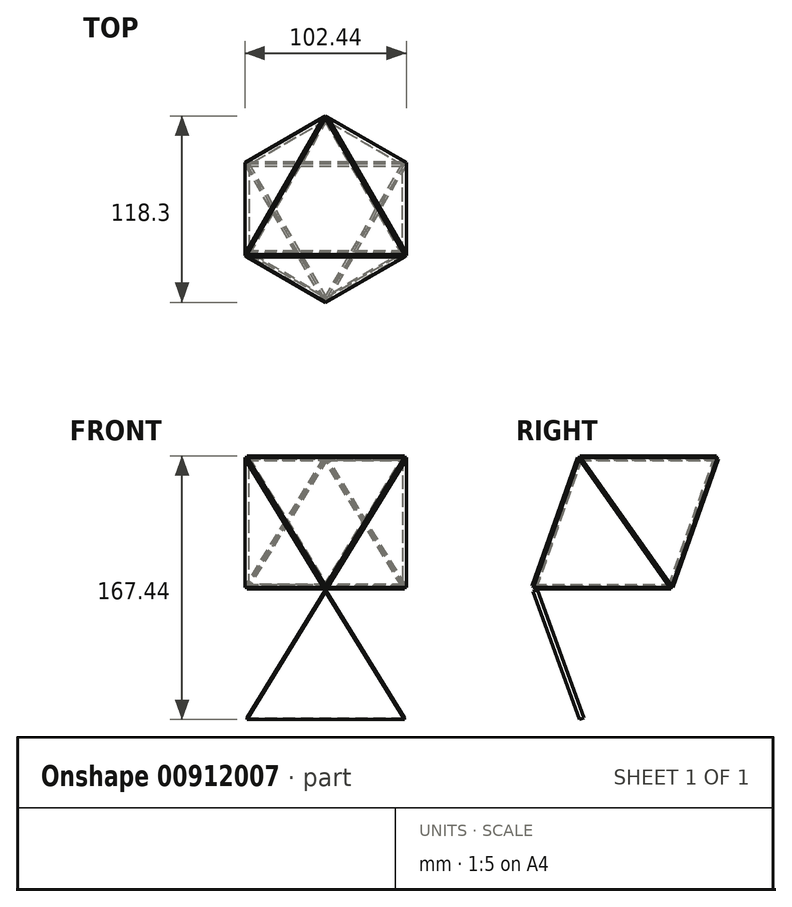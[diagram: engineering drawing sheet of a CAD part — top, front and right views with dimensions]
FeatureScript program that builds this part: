
annotation { "Feature Type Name" : "Feature", "Feature Type Description" : "" }
export const myFeature = defineFeature(function(context is Context, id is Id, definition is map)
    precondition{}
    {
        {
            var Q0;
            Q0=qCreatedBy(makeId("Top.planeOp"),FACE);
            var sketch = newSketch(context, id + "F0", { "sketchPlane" : qUnion([Q0])});
            skCircle(sketch, "E0.cCircle", {"center": v(0, 0) * mm, "radius": 28.87 * mm, "construction": true});
            skLineSegment(sketch, "E0.0", {"start": v(-50, 28.87) * mm, "end": v(50, 28.87) * mm});
            skLineSegment(sketch, "E0.1", {"start": v(50, 28.87) * mm, "end": v(0, -57.74) * mm});
            skLineSegment(sketch, "E0.2", {"start": v(0, -57.74) * mm, "end": v(-50, 28.87) * mm});
            skPoint(sketch, "E0.0.midPoint", {"position": v(0, 28.87) * mm});
            skSolve(sketch);
        }
        {
            var Q0;
            Q0=makeQuery(id+"F0.imprint","IMPRINT",FACE,{"disambiguationData":[TD([[makeQuery(id+"F0.imprint","IMPRINT",EDGE,{"derivedFrom":sQuery(id+"F0.wireOp",EDGE,"E0.0")}),-1.0]])]});
            extrude(context, id + "F1", {"entities" : qUnion([Q0]), "depth" : 3 * mm, "offsetDistance" : 25 * mm});
        }
        {
            var Q0;
            Q0=makeQuery(id+"F1.opExtrude","SWEPT_FACE",FACE,{"disambiguationData":[OSD([sQuery(id+"F0.wireOp",EDGE,"E0.2")])]});
            var sketch = newSketch(context, id + "F2", { "sketchPlane" : qUnion([Q0])});
            skLineSegment(sketch, "E1", {"start": v(-50, 1.5) * mm, "end": v(50, 1.5) * mm});
            skSolve(sketch);
        }
        {
            var Q0;
            Q0=makeQuery(id+"F1.opExtrude","SWEPT_BODY",BODY,{"disambiguationData":[OSD([sQuery(id+"F0.wireOp",EDGE,"E0.0"),sQuery(id+"F0.wireOp",EDGE,"E0.1"),sQuery(id+"F0.wireOp",EDGE,"E0.2")])]});
            transform(context, id + "F3", {"entities" : qUnion([Q0]), "transformType" : TransformType.TRANSLATION_3D, "dx" : 0 * mm, "dy" : 0 * mm, "dz" : 0 * mm, "makeCopy" : true});
        }
        {
            var Q0;
            Q0=makeQuery(id+"F3.opPattern","COPY",BODY,{"derivedFrom":makeQuery(id+"F1.opExtrude","SWEPT_BODY",BODY,{"disambiguationData":[OSD([sQuery(id+"F0.wireOp",EDGE,"E0.0"),sQuery(id+"F0.wireOp",EDGE,"E0.1"),sQuery(id+"F0.wireOp",EDGE,"E0.2")])]}),"instanceName":"1"});
            var Q1;
            Q1=sQuery(id+"F2.wireOp",EDGE,"E1");
            var Q2;
            Q2=sQuery(id+"F2.wireOp",EDGE,"E1");
            transform(context, id + "F4", {"entities" : qUnion([Q0]), "transformType" : TransformType.ROTATION, "transformAxis" : qUnion([Q2]), "angle" : 109.47 * degree, "makeCopy" : false});
        }
        {
            var Q0;
            Q0=makeQuery(id+"F1.opExtrude","SWEPT_BODY",BODY,{"disambiguationData":[OSD([sQuery(id+"F0.wireOp",EDGE,"E0.0"),sQuery(id+"F0.wireOp",EDGE,"E0.1"),sQuery(id+"F0.wireOp",EDGE,"E0.2")])]});
            transform(context, id + "F5", {"entities" : qUnion([Q0]), "transformType" : TransformType.TRANSLATION_3D, "dx" : 0 * mm, "dy" : 0 * mm, "dz" : 0 * mm, "makeCopy" : true});
        }
        {
            var Q0;
            Q0=makeQuery(id+"F1.opExtrude","SWEPT_FACE",FACE,{"disambiguationData":[OSD([sQuery(id+"F0.wireOp",EDGE,"E0.0")])]});
            var sketch = newSketch(context, id + "F6", { "sketchPlane" : qUnion([Q0])});
            skLineSegment(sketch, "E2", {"start": v(50, 1.5) * mm, "end": v(-50, 1.5) * mm});
            skSolve(sketch);
        }
        {
            var Q0;
            Q0=makeQuery(id+"F5.opPattern","COPY",BODY,{"derivedFrom":makeQuery(id+"F1.opExtrude","SWEPT_BODY",BODY,{"disambiguationData":[OSD([sQuery(id+"F0.wireOp",EDGE,"E0.0"),sQuery(id+"F0.wireOp",EDGE,"E0.1"),sQuery(id+"F0.wireOp",EDGE,"E0.2")])]}),"instanceName":"1"});
            var Q1;
            Q1=sQuery(id+"F6.wireOp",EDGE,"E2");
            var Q2;
            Q2=sQuery(id+"F6.wireOp",EDGE,"E2");
            transform(context, id + "F7", {"entities" : qUnion([Q0]), "transformType" : TransformType.ROTATION, "transformAxis" : qUnion([Q2]), "angle" : 109.47 * degree, "oppositeDirection" : true, "makeCopy" : false});
        }
        {
            var Q0;
            Q0=qCreatedBy(makeId("Front.planeOp"),FACE);
            var sketch = newSketch(context, id + "F8", { "sketchPlane" : qUnion([Q0])});
            skLineSegment(sketch, "E3", {"start": v(0, 0) * mm, "end": v(0, 75.98) * mm});
            skSolve(sketch);
        }
        {
            var Q0;
            Q0=makeQuery(id+"F3.opPattern","COPY",BODY,{"derivedFrom":makeQuery(id+"F1.opExtrude","SWEPT_BODY",BODY,{"disambiguationData":[OSD([sQuery(id+"F0.wireOp",EDGE,"E0.0"),sQuery(id+"F0.wireOp",EDGE,"E0.1"),sQuery(id+"F0.wireOp",EDGE,"E0.2")])]}),"instanceName":"1"});
            var Q1;
            Q1=sQuery(id+"F8.wireOp",EDGE,"E3");
            circularPattern(context, id + "F9", {"entities" : qUnion([Q0]), "axis" : qUnion([Q1]), "angle" : 360 * degree, "instanceCount" : 3, "equalSpace" : true});
        }
        {
            var Q0;
            Q0=makeQuery(id+"F5.opPattern","COPY",FACE,{"derivedFrom":makeQuery(id+"F1.opExtrude","SWEPT_FACE",FACE,{"disambiguationData":[OSD([sQuery(id+"F0.wireOp",EDGE,"E0.1")])]}),"instanceName":"1"});
            var sketch = newSketch(context, id + "F10", { "sketchPlane" : qUnion([Q0])});
            skLineSegment(sketch, "E4", {"start": v(21.03, -22.59) * mm, "end": v(50.3, 73.03) * mm});
            skSolve(sketch);
        }
        {
            var Q0;
            Q0=makeQuery(id+"F5.opPattern","COPY",BODY,{"derivedFrom":makeQuery(id+"F1.opExtrude","SWEPT_BODY",BODY,{"disambiguationData":[OSD([sQuery(id+"F0.wireOp",EDGE,"E0.0"),sQuery(id+"F0.wireOp",EDGE,"E0.1"),sQuery(id+"F0.wireOp",EDGE,"E0.2")])]}),"instanceName":"1"});
            var Q1;
            Q1=sQuery(id+"F10.wireOp",EDGE,"E4");
            transform(context, id + "F11", {"entities" : qUnion([Q0]), "transformType" : TransformType.ROTATION, "transformAxis" : qUnion([Q1]), "angle" : 109.47 * degree, "makeCopy" : false});
        }
        {
            var Q0;
            Q0=makeQuery(id+"F5.opPattern","COPY",BODY,{"derivedFrom":makeQuery(id+"F1.opExtrude","SWEPT_BODY",BODY,{"disambiguationData":[OSD([sQuery(id+"F0.wireOp",EDGE,"E0.0"),sQuery(id+"F0.wireOp",EDGE,"E0.1"),sQuery(id+"F0.wireOp",EDGE,"E0.2")])]}),"instanceName":"1"});
            var Q1;
            Q1=sQuery(id+"F8.wireOp",EDGE,"E3");
            circularPattern(context, id + "F12", {"entities" : qUnion([Q0]), "axis" : qUnion([Q1]), "angle" : 360 * degree, "instanceCount" : 3, "equalSpace" : true});
        }
        {
            var Q0;
            Q0=makeQuery(id+"F5.opPattern","COPY",FACE,{"derivedFrom":makeQuery(id+"F1.opExtrude","SWEPT_FACE",FACE,{"disambiguationData":[OSD([sQuery(id+"F0.wireOp",EDGE,"E0.2")])]}),"instanceName":"1"});
            var sketch = newSketch(context, id + "F13", { "sketchPlane" : qUnion([Q0])});
            skLineSegment(sketch, "E5", {"start": v(20.74, 71.33) * mm, "end": v(72.96, -13.95) * mm});
            skSolve(sketch);
        }
        {
            var Q0;
            Q0=makeQuery(id+"F5.opPattern","COPY",BODY,{"derivedFrom":makeQuery(id+"F1.opExtrude","SWEPT_BODY",BODY,{"disambiguationData":[OSD([sQuery(id+"F0.wireOp",EDGE,"E0.0"),sQuery(id+"F0.wireOp",EDGE,"E0.1"),sQuery(id+"F0.wireOp",EDGE,"E0.2")])]}),"instanceName":"1"});
            transform(context, id + "F14", {"entities" : qUnion([Q0]), "transformType" : TransformType.TRANSLATION_3D, "dx" : 0 * mm, "dy" : 0 * mm, "dz" : 0 * mm, "makeCopy" : true});
        }
        {
            var Q0;
            Q0=makeQuery(id+"F14.opPattern","COPY",BODY,{"derivedFrom":makeQuery(id+"F5.opPattern","COPY",BODY,{"derivedFrom":makeQuery(id+"F1.opExtrude","SWEPT_BODY",BODY,{"disambiguationData":[OSD([sQuery(id+"F0.wireOp",EDGE,"E0.0"),sQuery(id+"F0.wireOp",EDGE,"E0.1"),sQuery(id+"F0.wireOp",EDGE,"E0.2")])]}),"instanceName":"1"}),"instanceName":"1"});
            var Q1;
            Q1=sQuery(id+"F13.wireOp",EDGE,"E5");
            var Q2;
            Q2=sQuery(id+"F13.wireOp",EDGE,"E5");
            transform(context, id + "F15", {"entities" : qUnion([Q0]), "transformType" : TransformType.ROTATION, "transformAxis" : qUnion([Q2]), "angle" : 109.47 * degree, "oppositeDirection" : true, "makeCopy" : false});
        }
        {
            var Q0;
            Q0=qCreatedBy(makeId("Right.planeOp"),FACE);
            var sketch = newSketch(context, id + "F16", { "sketchPlane" : qUnion([Q0])});
            skLineSegment(sketch, "E6", {"start": v(-59.2, 0) * mm, "end": v(31.56, 0) * mm});
            skSolve(sketch);
        }
        {
            var Q0;
            Q0=sQuery(id+"F16.wireOp",VERTEX,"E6.start");
            var Q1;
            Q1=sQuery(id+"F16.wireOp",EDGE,"E6");
            cPlane(context, id + "F17", {"entities" : qUnion([Q0, Q1]), "cplaneType" : CPlaneType.LINE_POINT, "offset" : 25 * mm, "width" : 150 * mm, "height" : 150 * mm});
        }
        {
            var Q0;
            Q0=makeQuery(id+"F1.opExtrude","SWEPT_BODY",BODY,{"disambiguationData":[OSD([sQuery(id+"F0.wireOp",EDGE,"E0.0"),sQuery(id+"F0.wireOp",EDGE,"E0.1"),sQuery(id+"F0.wireOp",EDGE,"E0.2")])]});
            transform(context, id + "F18", {"entities" : qUnion([Q0]), "transformType" : TransformType.TRANSLATION_3D, "dx" : 0 * mm, "dy" : 0 * mm, "dz" : 0 * mm, "makeCopy" : true});
        }
        {
            var Q0;
            Q0=qCreatedBy(makeId("Top.planeOp"),FACE);
            var sketch = newSketch(context, id + "F19", { "sketchPlane" : qUnion([Q0])});
            skLineSegment(sketch, "E7", {"start": v(0, -59.23) * mm, "end": v(49.37, -59.23) * mm});
            skSolve(sketch);
        }
        {
            var Q0;
            Q0=makeQuery(id+"F18.opPattern","COPY",BODY,{"derivedFrom":makeQuery(id+"F1.opExtrude","SWEPT_BODY",BODY,{"disambiguationData":[OSD([sQuery(id+"F0.wireOp",EDGE,"E0.0"),sQuery(id+"F0.wireOp",EDGE,"E0.1"),sQuery(id+"F0.wireOp",EDGE,"E0.2")])]}),"instanceName":"1"});
            var Q1;
            Q1=sQuery(id+"F19.wireOp",EDGE,"E7");
            transform(context, id + "F20", {"entities" : qUnion([Q0]), "transformType" : TransformType.ROTATION, "transformAxis" : qUnion([Q1]), "angle" : 70 * degree, "oppositeDirection" : true, "makeCopy" : false});
        }
    });
